# Revit family: Pelée385_17W_3000K_LOD 300
name_source: partatom
category: Lighting Fixtures
revit_build: Autodesk Revit 2015 (Build: 20140606_1530(x64)
units: mm (PartAtom-declared; Revit-internal decimal feet)

## types (1)
- Pelée 385_17,4W_3000K
    CRI = 80
    Color Filter = 16777215
    Date = 05.03.2015
    Description = Pelée 385_17,4W_3000K
    Diffuser Material = Glass, White, High Luminance
    Dimming Lamp Color Temperature Shift = <None>
    Indbygningshøjde = 0 mm  [stored 0 ft]
    Light Downwards Output Ratio = 81 %
    Light Sources = 1
    Light Sources Type = CLEg2-315-4000-830_500mA
    Light Total Output Ratio = 81.7 %
    Manufacturer = Focus Lighting A/S
    Material = Aluminum-Focus Lighting-Pelee 385-Semi-Polished
    Model = Version 1
    Nominal Height = 91 mm
    Nominal Width = 385 mm
    Photometric Web File = Pelèe 385_17,4W_3000K.ies
    Product Family = Indoors
    Product Group = Loft- & Indbygningslamper
    Revit Object URL = http://www.newbim.info
    Tilt Angle = 60.00°
    Type Image = Perspective View 2.PNG
    URL = http://focus-lighting.dk
    Watt total = 17.4 W

note: [stored X ft] marks values corroborated as IEEE doubles in the binary element streams (Revit-internal decimal feet)

## geometry (parser evidence)
native form markers: Blend x4, Extrusion x1, Sweep x2
no freeform markers — native parametric forms only
